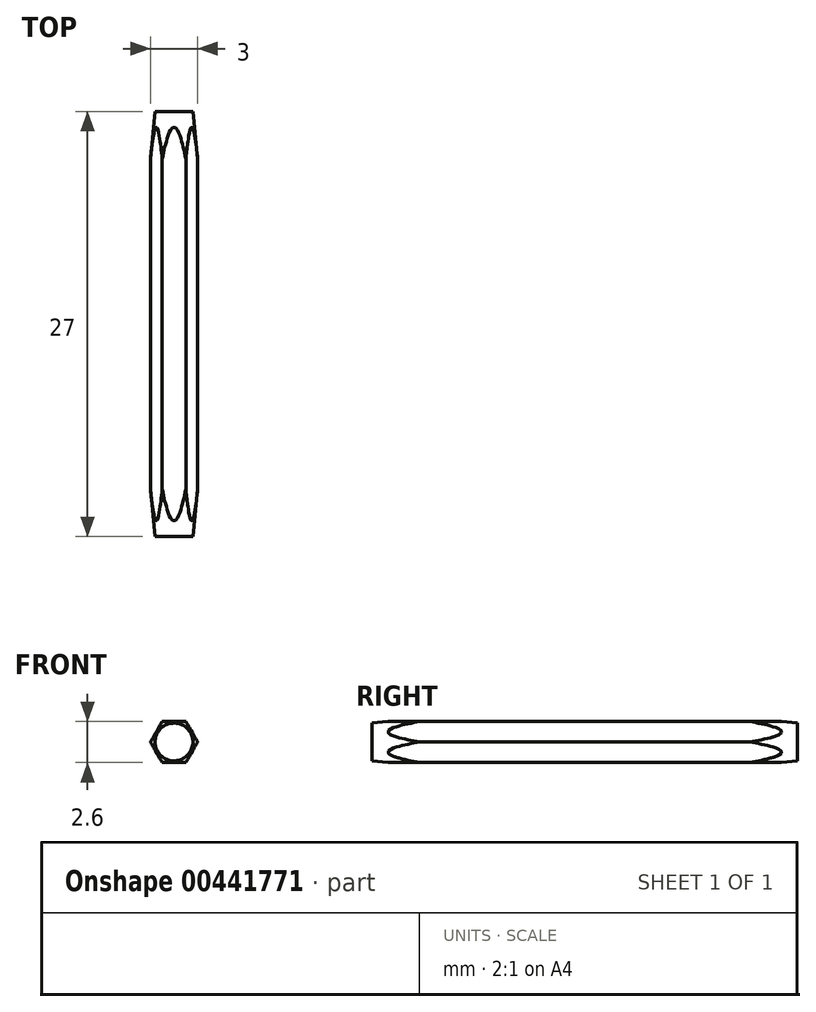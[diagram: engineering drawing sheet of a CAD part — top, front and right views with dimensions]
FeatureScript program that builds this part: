
annotation { "Feature Type Name" : "Feature", "Feature Type Description" : "" }
export const myFeature = defineFeature(function(context is Context, id is Id, definition is map)
    precondition{}
    {
        {
            var Q0;
            Q0=qCreatedBy(makeId("Front.planeOp"),FACE);
            var sketch = newSketch(context, id + "F0", { "sketchPlane" : qUnion([Q0])});
            skCircle(sketch, "E0.cCircle", {"center": v(0, 0) * mm, "radius": 1.5 * mm, "construction": true});
            skLineSegment(sketch, "E0.0", {"start": v(-1.5, 0) * mm, "end": v(-0.75, 1.3) * mm});
            skLineSegment(sketch, "E0.1", {"start": v(-0.75, 1.3) * mm, "end": v(0.75, 1.3) * mm});
            skLineSegment(sketch, "E0.2", {"start": v(0.75, 1.3) * mm, "end": v(1.5, 0) * mm});
            skLineSegment(sketch, "E0.3", {"start": v(1.5, 0) * mm, "end": v(0.75, -1.3) * mm});
            skLineSegment(sketch, "E0.4", {"start": v(0.75, -1.3) * mm, "end": v(-0.75, -1.3) * mm});
            skLineSegment(sketch, "E0.5", {"start": v(-0.75, -1.3) * mm, "end": v(-1.5, 0) * mm});
            skSolve(sketch);
        }
        {
            var Q0;
            Q0=qSketchRegion(id+"F0",true);
            extrude(context, id + "F1", {"entities" : qUnion([Q0]), "depth" : (27 / 2) * mm});
        }
        {
            var Q0;
            Q0=qCreatedBy(makeId("Right.planeOp"),FACE);
            var sketch = newSketch(context, id + "F2", { "sketchPlane" : qUnion([Q0])});
            skLineSegment(sketch, "E1", {"start": v(-13.5, 1.2) * mm, "end": v(-12.5, 1.3) * mm});
            skLineSegment(sketch, "E2", {"start": v(0, 0) * mm, "end": v(15.07, 0) * mm});
            skLineSegment(sketch, "E3", {"start": v(-12.5, 1.3) * mm, "end": v(-0.63, 2.47) * mm});
            skLineSegment(sketch, "E4", {"start": v(-0.63, 2.47) * mm, "end": v(-15.53, 2.47) * mm});
            skLineSegment(sketch, "E5", {"start": v(-15.53, 2.47) * mm, "end": v(-15.53, 1) * mm});
            skLineSegment(sketch, "E6", {"start": v(-15.53, 1) * mm, "end": v(-13.5, 1.2) * mm});
            skSolve(sketch);
        }
        {
            var Q0;
            Q0=makeQuery(id+"F2.imprint","IMPRINT",FACE,{"disambiguationData":[TD([[makeQuery(id+"F2.imprint","IMPRINT",EDGE,{"derivedFrom":sQuery(id+"F2.wireOp",EDGE,"E1")}),1.0]])]});
            var Q1;
            Q1=sQuery(id+"F2.wireOp",EDGE,"E2");
            revolve(context, id + "F3", {"operationType" : NewBodyOperationType.REMOVE, "entities" : qUnion([Q0]), "axis" : qUnion([Q1]), "revolveType" : RevolveType.FULL, "oppositeDirection" : true});
        }
        {
            var Q0;
            Q0=makeQuery(id+"F1.opExtrude","SWEPT_BODY",BODY,{"disambiguationData":[OSD([sQuery(id+"F0.wireOp",EDGE,"E0.0"),sQuery(id+"F0.wireOp",EDGE,"E0.1"),sQuery(id+"F0.wireOp",EDGE,"E0.2"),sQuery(id+"F0.wireOp",EDGE,"E0.3"),sQuery(id+"F0.wireOp",EDGE,"E0.4"),sQuery(id+"F0.wireOp",EDGE,"E0.5")])]});
            var Q1;
            Q1=qCreatedBy(makeId("Front.planeOp"),FACE);
            mirror(context, id + "F4", {"operationType" : NewBodyOperationType.ADD, "entities" : qUnion([Q0]), "mirrorPlane" : qUnion([Q1])});
        }
    });
